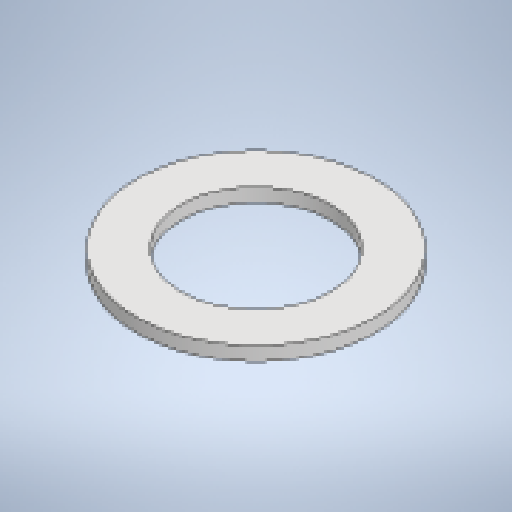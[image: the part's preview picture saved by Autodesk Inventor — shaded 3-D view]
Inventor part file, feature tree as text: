
AUTODESK INVENTOR PART (.ipt)
format: ipt  version: 2025 (Build 290162010, 162A)  size: 177,152 bytes
history: native  units: mm
features: other x2, sheet_metal_op x1, sketch x1
ambient origin geometry x8: Origin, YZ Plane, XZ Plane, XY Plane, X Axis, Y Axis, Z Axis, Center Point
bodies: Body1 (feature_tree)
feature tree (4):
  sheet_metal_op  "Face2"
  sketch  "Sketch2"  dims[d14=8.0mm d25=88.0mm d27=140.0mm]
  other  "Plate2"
  other  "Definition1"
